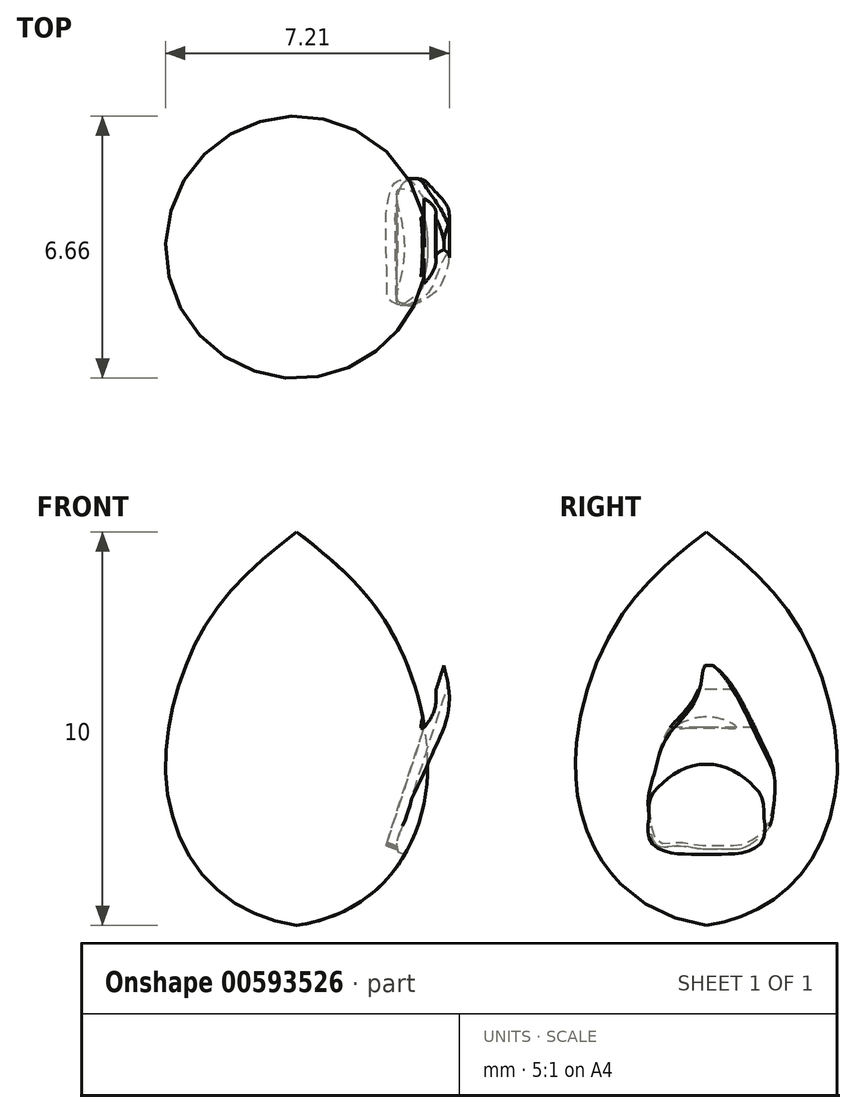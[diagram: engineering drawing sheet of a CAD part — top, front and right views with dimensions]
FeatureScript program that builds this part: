
annotation { "Feature Type Name" : "Feature", "Feature Type Description" : "" }
export const myFeature = defineFeature(function(context is Context, id is Id, definition is map)
    precondition{}
    {
        {
            var Q0;
            Q0=qCreatedBy(makeId("Front.planeOp"),FACE);
            var sketch = newSketch(context, id + "F0", { "sketchPlane" : qUnion([Q0])});
            skLineSegment(sketch, "E0", {"start": v(0, 5) * mm, "end": v(0, -5) * mm});
            skPoint(sketch, "E1", {"position": v(0, 0) * mm});
            skFitSpline(sketch, "E2", {"points": [v(0, -5) * mm, v(2.13, -4) * mm, v(3.32, -1.3) * mm, v(2.44, 2.4) * mm, v(0, 5) * mm], "startDerivative": vector(10.86, 1.58) * mm, "endDerivative": vector(-12.82, 9.94) * mm});
            skSolve(sketch);
        }
        {
            var Q0;
            Q0=makeQuery(id+"F0.imprint","IMPRINT",FACE,{"disambiguationData":[TD([[makeQuery(id+"F0.imprint","IMPRINT",EDGE,{"derivedFrom":sQuery(id+"F0.wireOp",EDGE,"E0")}),1.0]])]});
            var Q1;
            Q1=sQuery(id+"F0.wireOp",EDGE,"E0");
            revolve(context, id + "F1", {"entities" : qUnion([Q0]), "axis" : qUnion([Q1]), "revolveType" : RevolveType.FULL});
        }
        {
            var Q0;
            Q0=qCreatedBy(makeId("Front.planeOp"),FACE);
            var sketch = newSketch(context, id + "F2", { "sketchPlane" : qUnion([Q0])});
            skPoint(sketch, "E3", {"position": v(1.84, -4.26) * mm});
            skLineSegment(sketch, "E4", {"start": v(0.73, -4.97) * mm, "end": v(2.18, -4.05) * mm});
            skLineSegment(sketch, "E5", {"start": v(1.84, -4.26) * mm, "end": v(1.2, -3.24) * mm});
            skSolve(sketch);
        }
        {
            var Q0;
            Q0=sQuery(id+"F2.wireOp",EDGE,"E5");
            var Q1;
            Q1=sQuery(id+"F2.wireOp",VERTEX,"E3");
            var Q2;
            Q2 = qBodyType(qCreatedBy(id + "F4" ,EDGE), BodyType.WIRE);
            cPlane(context, id + "F3", {"entities" : qUnion([Q0, Q1, Q2]), "cplaneType" : CPlaneType.LINE_POINT, "offset" : 25 * mm, "width" : 150 * mm, "height" : 150 * mm});
        }
        {
            var Q0;
            Q0=qCreatedBy(id+"F3.planeOp",FACE);
            var sketch = newSketch(context, id + "F4", { "sketchPlane" : qUnion([Q0])});
            skFitSpline(sketch, "E6", {"points": [v(-1.74, -1.23) * mm, v(-1.74, -0.74) * mm, v(-1.8, -0.29) * mm, v(-1.82, 0) * mm, v(-1.82, 0.32) * mm, v(-1.82, 0.72) * mm, v(-1.8, 0.92) * mm, v(-1.36, 1.51) * mm, v(-0.8, 1.7) * mm, v(0.15, 1.73) * mm, v(0.84, 1.47) * mm, v(1.59, 1.14) * mm, v(2.6, 0.56) * mm, v(3.06, 0) * mm, v(2.4, -0.2) * mm, v(1.33, -0.95) * mm, v(0.68, -1.22) * mm, v(0.08, -1.37) * mm, v(-0.48, -1.48) * mm, v(-1.16, -1.43) * mm, v(-1.74, -1.23) * mm]});
            skSolve(sketch);
        }
        {
            var Q0;
            Q0=qCreatedBy(makeId("Right.planeOp"),FACE);
            var sketch = newSketch(context, id + "F5", { "sketchPlane" : qUnion([Q0])});
            skLineSegment(sketch, "E7", {"start": v(-8.35, 0) * mm, "end": v(15.1, 0) * mm});
            skSolve(sketch);
        }
        {
            var Q0;
            Q0 = qSketchRegion(id + "F4", true);
            extrude(context, id + "F6", {"entities" : qUnion([Q0]), "endBound" : BoundingType.SYMMETRIC, "depth" : 0.5 * mm, "offsetDistance" : 25 * mm, "hasDraft" : true, "draftAngle" : 3 * degree, "draftPullDirection" : true});
        }
        {
            var Q0;
            Q0=makeQuery(id+"F6.opExtrude","SWEPT_BODY",BODY,{"disambiguationData":[OSD([sQuery(id+"F4.wireOp",EDGE,"E6")])]});
            transform(context, id + "F7", {"entities" : qUnion([Q0]), "transformType" : TransformType.TRANSLATION_3D, "dx" : -0.95 * mm, "dy" : 0 * mm, "dz" : 0.9 * mm, "makeCopy" : false});
        }
        {
            var Q0;
            Q0=makeQuery(id+"F6.opExtrude","SWEPT_BODY",BODY,{"disambiguationData":[OSD([sQuery(id+"F4.wireOp",EDGE,"E6")])]});
            var Q1;
            Q1=sQuery(id+"F5.wireOp",EDGE,"E7");
            transform(context, id + "F8", {"entities" : qUnion([Q0]), "transformType" : TransformType.ROTATION, "transformAxis" : qUnion([Q1]), "angle" : 40 * degree, "oppositeDirection" : true, "makeCopy" : false});
        }
        {
            var Q0;
            Q0=qCreatedBy(makeId("Front.planeOp"),FACE);
            var sketch = newSketch(context, id + "F9", { "sketchPlane" : qUnion([Q0])});
            skFitSpline(sketch, "E8", {"points": [v(2.93, -1.78) * mm, v(3.11, -1.4) * mm, v(3.48, -0.57) * mm, v(3.8, 0.17) * mm, v(3.85, 1.15) * mm, v(3.78, 1.8) * mm, v(4.37, 1.5) * mm, v(4.38, 0.92) * mm, v(3.72, -1.05) * mm, v(2.78, -3.18) * mm, v(2.55, -3.03) * mm, v(2.77, -2.29) * mm, v(2.93, -1.78) * mm]});
            skFitSpline(sketch, "E9", {"points": [v(3.74, 1.73) * mm, v(3.55, 1.04) * mm, v(3.54, 0.68) * mm, v(3.42, 0.3) * mm, v(3.18, 0) * mm, v(3.4, 0.88) * mm, v(3.74, 1.73) * mm]});
            skSolve(sketch);
        }
        {
            var Q0;
            Q0 = qSketchRegion(id + "F9", true);
            extrude(context, id + "F10", {"entities" : qUnion([Q0]), "operationType" : NewBodyOperationType.REMOVE, "endBound" : BoundingType.SYMMETRIC, "oppositeDirection" : true, "depth" : 3.5 * mm, "offsetDistance" : 25 * mm});
        }
    });
